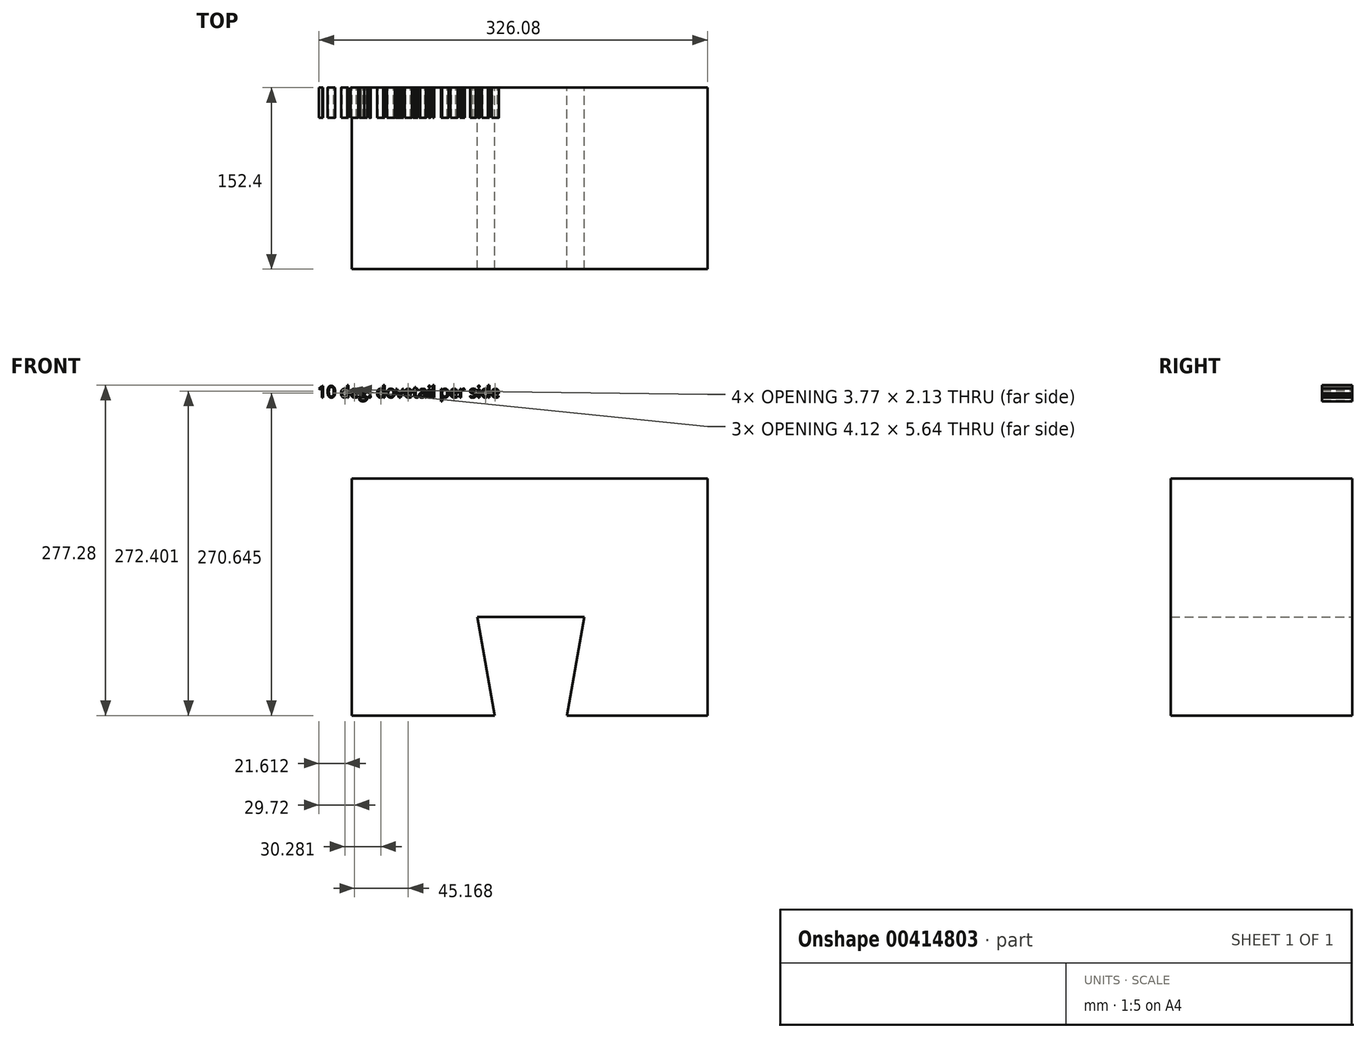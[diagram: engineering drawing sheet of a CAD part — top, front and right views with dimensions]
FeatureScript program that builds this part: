
annotation { "Feature Type Name" : "Feature", "Feature Type Description" : "" }
export const myFeature = defineFeature(function(context is Context, id is Id, definition is map)
    precondition{}
    {
        {
            var Q0;
            Q0=qCreatedBy(makeId("Front.planeOp"),FACE);
            var sketch = newSketch(context, id + "F0", { "sketchPlane" : qUnion([Q0])});
            skLineSegment(sketch, "E0.bottom", {"start": v(149.25, -99.44) * mm, "end": v(-149.25, -99.44) * mm});
            skLineSegment(sketch, "E0.top", {"start": v(149.25, 99.44) * mm, "end": v(-149.25, 99.44) * mm});
            skLineSegment(sketch, "E0.left", {"start": v(149.25, -99.44) * mm, "end": v(149.25, 99.44) * mm});
            skLineSegment(sketch, "E0.right", {"start": v(-149.25, -99.44) * mm, "end": v(-149.25, 99.44) * mm});
            skPoint(sketch, "E0.middle", {"position": v(0, 0) * mm});
            skLineSegment(sketch, "E1", {"start": v(-29.49, -99.44) * mm, "end": v(-44.07, -16.75) * mm});
            skLineSegment(sketch, "E2", {"start": v(-44.07, -16.75) * mm, "end": v(45.92, -16.75) * mm});
            skLineSegment(sketch, "E3", {"start": v(45.92, -16.75) * mm, "end": v(31.34, -99.44) * mm});
            skSolve(sketch);
        }
        {
            var Q0;
            Q0=makeQuery(id+"F0.imprint","IMPRINT",FACE,{"disambiguationData":[TD([[makeQuery(id+"F0.imprint","IMPRINT",EDGE,{"derivedFrom":sQuery(id+"F0.wireOp",EDGE,"E0.top")}),1.0]])]});
            extrude(context, id + "F1", {"entities" : qUnion([Q0]), "depth" : 152.4 * mm});
        }
        {
            var Q0;
            Q0=qCreatedBy(makeId("Front.planeOp"),FACE);
            var sketch = newSketch(context, id + "F2", { "sketchPlane" : qUnion([Q0])});
            skText(sketch, "E4", { "text": "10 deg. dovetail per side", "fontName": "OpenSans-Regular.ttf"});
            const initialGuessF2  = {"E4": [-0.17807, 0.1676, 1, 0, 0.0097]};
            skSetInitialGuess(sketch, initialGuessF2);
            skSolve(sketch);
        }
        {
            var Q0;
            Q0 = qSketchRegion(id + "F2", true);
            extrude(context, id + "F3", {"entities" : qUnion([Q0]), "depth" : 25.4 * mm});
        }
    });
